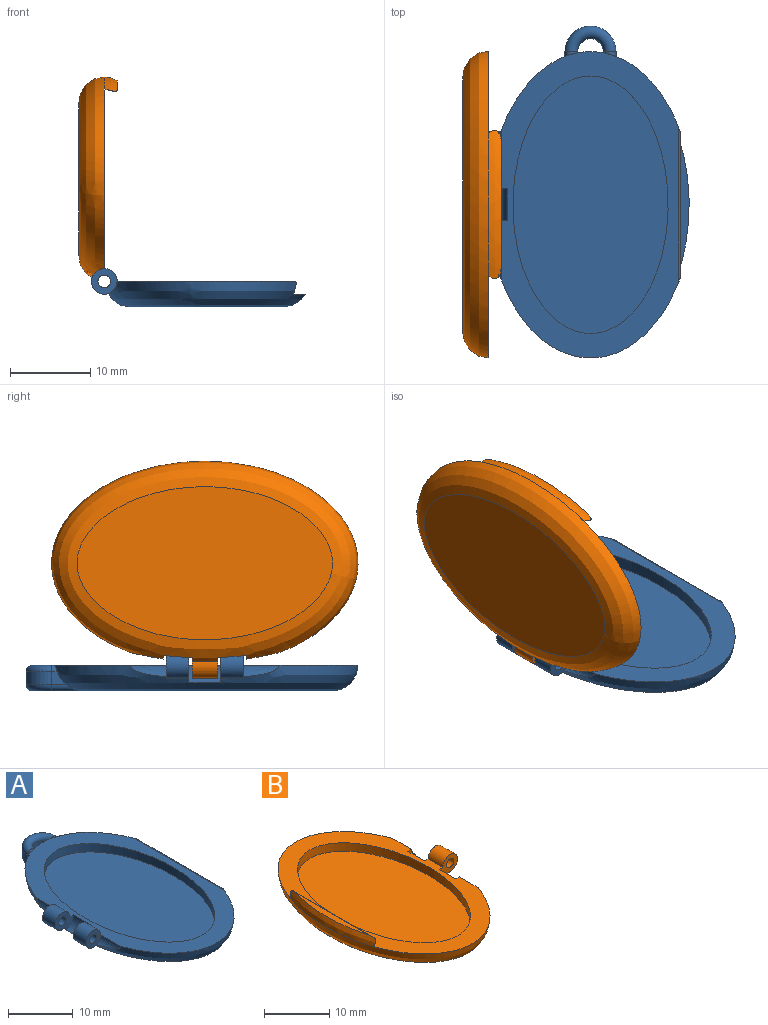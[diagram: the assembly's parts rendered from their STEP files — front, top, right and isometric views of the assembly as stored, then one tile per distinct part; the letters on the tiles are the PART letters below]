
ASSEMBLY  parts=2 mates=1
PART A: 33 faces, bbox 27.1x41.7x4.9 mm
  f0: bspline ~38.1x25.41mm, area 394.2mm2, adj f1,f3,f5,f8,f9,f10,f13,f14
  f1: plane 38.14x22.07mm, normal (0,0,1), area 228.3mm2, adj f0,f3,f6,f10,f13,f14,f15,f16
  f2: cylinder r=0.79mm len=2.78mm, axis (0,1,0), area 13.9mm2, adj f12,f16
  f3: cylinder r=1.59mm len=3.18mm, axis (0,-1,0), area 22.5mm2, adj f0,f1,f12,f16
  f4: cylinder r=0.79mm len=2.78mm, axis (0,1,0), area 13.9mm2, adj f11,f17
  f5: plane 31.75x19.06mm, normal (0,0,-1), area 472.1mm2, adj f0
  f6: extruded ~32x19.3mm, area 129.9mm2, adj f1,f7
  f7: plane 32x19.3mm, normal (0,0,1), area 485.2mm2, adj f6
  f8: plane 18.33x1.27mm, normal (0.97,0,-0.26), area 23.8mm2, adj f0,f9,f32
  f9: plane 17.65x1.52mm, normal (0,0,1), area 17.3mm2, adj f0,f8
  f10: cylinder r=1.59mm len=3.18mm, axis (0,1,0), area 22.5mm2, adj f0,f1,f11,f17
  f11: plane 3.18x3.18mm, normal (0,-1,0), area 5.9mm2, adj f4,f10,f15
  f12: plane 3.18x3.18mm, normal (0,1,0), area 5.9mm2, adj f2,f3,f14
  f13: cylinder r=2.38mm len=3.97mm, axis (0,-1,0), area 11mm2, adj f0,f1,f16,f17
  f14: cylinder r=1.59mm len=4.46mm, axis (0,-1,0), area 3.9mm2, adj f0,f1,f12
  f15: cylinder r=1.59mm len=4.46mm, axis (0,1,0), area 3.9mm2, adj f0,f1,f11
  f16: plane 3.97x3.78mm, normal (0,-1,0), area 7.9mm2, adj f0,f1,f2,f3,f13
  f17: plane 3.97x3.78mm, normal (0,1,0), area 7.9mm2, adj f0,f1,f4,f10,f13
  f18: cylinder r=1.59mm len=3.18mm, axis (0,0,1), area 7.9mm2, adj f19,f25,f27,f30
  f19: plane 1.66x1.32mm, normal (-1,0,0), area 1mm2, adj f0,f18,f28,f31
  f20: extruded ~0.16x0.07mm, area 0mm2, adj f0,f31
  f21: plane 1.9x1.72mm, normal (1,0,0), area 1.8mm2, adj f0,f22,f28,f31
  f22: cylinder r=3.17mm len=6.35mm, axis (0,0,1), area 15.8mm2, adj f21,f23,f27,f30
  f23: plane 1.9x1.73mm, normal (-1,0,0), area 1.8mm2, adj f0,f22,f26,f29
  f24: extruded ~0.16x0.07mm, area 0mm2, adj f0,f29
  f25: plane 1.66x1.32mm, normal (1,0,0), area 1mm2, adj f0,f18,f26,f29
  f26: cylinder r=0.79mm len=1.59mm, axis (0,1,0), area 1mm2, adj f0,f23,f25,f27
  f27: torus R=2.38mm, axis (0,0,1), area 18.7mm2, adj f18,f22,f26,f28
  f28: cylinder r=0.79mm len=1.59mm, axis (0,-1,0), area 1mm2, adj f0,f19,f21,f27
  f29: cylinder r=0.79mm len=3.58mm, axis (0,-1,0), area 6.3mm2, adj f0,f23,f24,f25,f30
  f30: torus R=2.38mm, axis (0,0,1), area 18.7mm2, adj f18,f22,f29,f31
  f31: cylinder r=0.79mm len=3.58mm, axis (0,1,0), area 6.3mm2, adj f0,f19,f20,f21,f30
  f32: cylinder r=0.25mm len=19.51mm, axis (0,1,0), area 8.8mm2, adj f0,f1,f8
PART B: 19 faces, bbox 33.3x44.5x12.7 mm
  f0: plane 38.23x22.48mm, normal (0,0,1), area 231.7mm2, adj f1,f2,f5,f7,f9,f10,f11,f12
  f1: cylinder r=1.59mm len=4.06mm, axis (0,-1,0), area 3.4mm2, adj f0,f2,f16
  f2: bspline ~38.1x25.41mm, area 435.7mm2, adj f0,f1,f3,f4,f9,f10,f11,f12
  f3: plane 31.75x19.06mm, normal (0,0,-1), area 472.1mm2, adj f2
  f4: bspline ~21.22x5.12mm, area 30.4mm2, adj f2,f5,f6,f18
  f5: plane 18.4x1.27mm, normal (0.97,0,-0.26), area 23.9mm2, adj f0,f4,f18
  f6: plane 15.72x1.2mm, normal (0,0,1), area 12mm2, adj f4,f18
  f7: extruded ~32x19.3mm, area 129.9mm2, adj f0,f8
  f8: plane 32x19.3mm, normal (0,0,1), area 485.2mm2, adj f7
  f9: cylinder r=2.38mm len=3.57mm, axis (0,-1,0), area 9.4mm2, adj f0,f2,f10,f17
  f10: plane 10.32x10.13mm, normal (0,1,0), area 7.9mm2, adj f0,f2,f9,f14,f15
  f11: cylinder r=1.59mm len=4.06mm, axis (0,-1,0), area 3.4mm2, adj f0,f2,f17
  f12: cylinder r=2.38mm len=3.57mm, axis (0,1,0), area 9.4mm2, adj f0,f2,f13,f16
  f13: plane 3.98x3.79mm, normal (0,-1,0), area 7.9mm2, adj f0,f2,f12,f14,f15
  f14: cylinder r=1.59mm len=3.18mm, axis (0,1,0), area 33.1mm2, adj f0,f2,f10,f13
  f15: cylinder r=0.79mm len=3.18mm, axis (0,1,0), area 15.8mm2, adj f10,f13
  f16: plane 2.05x1.6mm, normal (0,1,0), area 1.6mm2, adj f0,f1,f2,f12
  f17: plane 2.05x1.6mm, normal (0,-1,0), area 1.6mm2, adj f0,f2,f9,f11
  f18: cylinder r=0.25mm len=18.14mm, axis (0,-1,0), area 7.9mm2, adj f4,f5,f6
PLACE A t=(-2.39,4.57,-3.13)mm
PLACE B rot(axis=(0,1,0),90deg) t=(-18.26,4.57,12.74)mm
MATE revolute B.f1 <-> A.f2  axis (0,1,0) through (-15.09,4.57,0.04)mm
